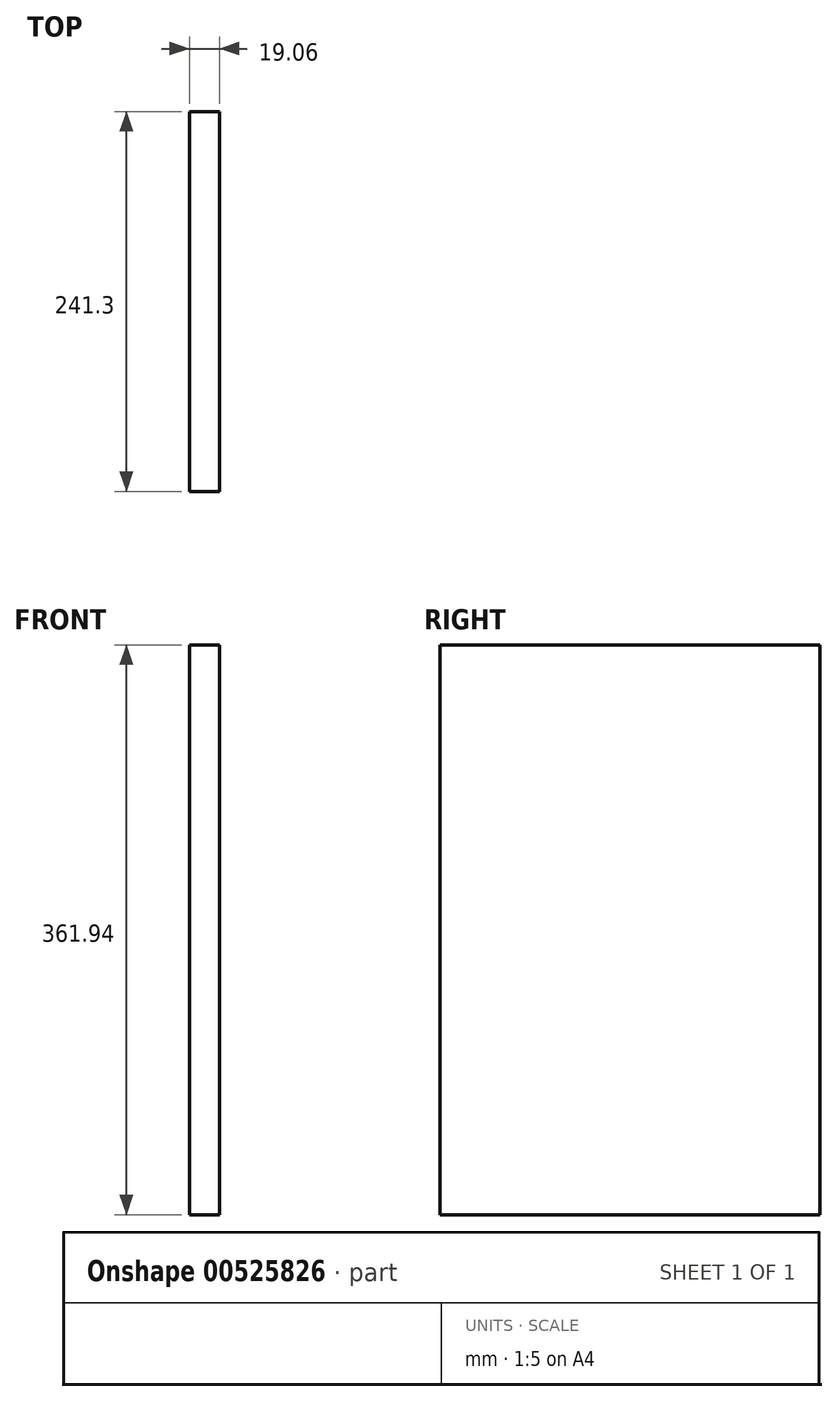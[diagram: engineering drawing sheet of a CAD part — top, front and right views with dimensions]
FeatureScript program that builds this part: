
annotation { "Feature Type Name" : "Feature", "Feature Type Description" : "" }
export const myFeature = defineFeature(function(context is Context, id is Id, definition is map)
    precondition{}
    {
        {
            var Q0;
            Q0=qCreatedBy(makeId("Front.planeOp"),FACE);
            var sketch = newSketch(context, id + "F0", { "sketchPlane" : qUnion([Q0])});
            skLineSegment(sketch, "E0.bottom", {"start": v(9.52, -180.98) * mm, "end": v(-9.53, -180.98) * mm});
            skLineSegment(sketch, "E0.top", {"start": v(9.53, 180.98) * mm, "end": v(-9.52, 180.98) * mm});
            skLineSegment(sketch, "E0.left", {"start": v(9.52, -180.98) * mm, "end": v(9.53, 180.98) * mm});
            skLineSegment(sketch, "E0.right", {"start": v(-9.53, -180.98) * mm, "end": v(-9.52, 180.98) * mm});
            skPoint(sketch, "E0.middle", {"position": v(0, 0) * mm});
            skSolve(sketch);
        }
        {
            var Q0;
            Q0=qSketchRegion(id+"F0",true);
            extrude(context, id + "F1", {"entities" : qUnion([Q0]), "depth" : 241.3 * mm});
        }
    });
